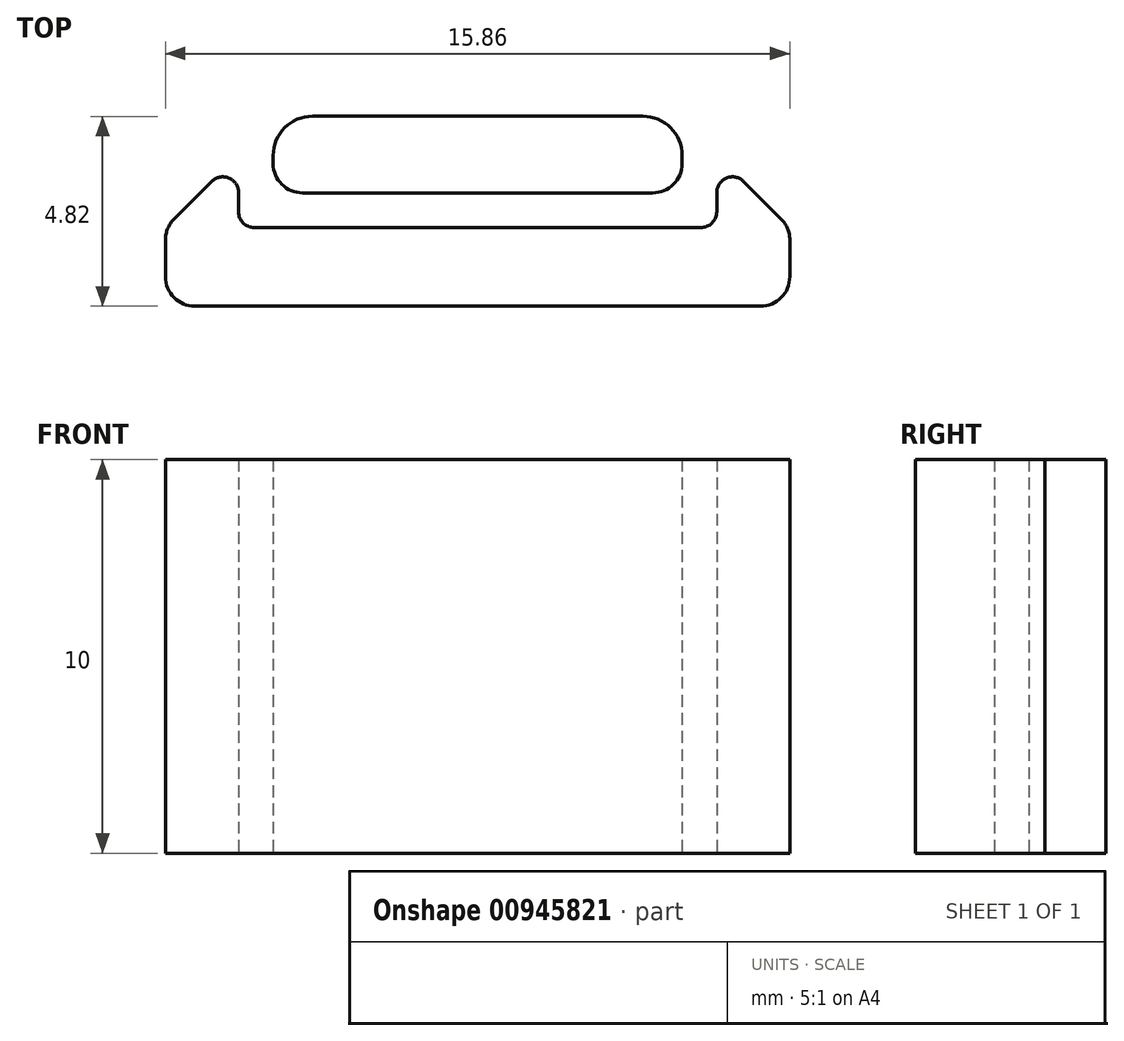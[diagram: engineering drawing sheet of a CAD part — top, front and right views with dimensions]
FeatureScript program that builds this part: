
annotation { "Feature Type Name" : "Feature", "Feature Type Description" : "" }
export const myFeature = defineFeature(function(context is Context, id is Id, definition is map)
    precondition{}
    {
        {
            var Q0;
            Q0=qCreatedBy(makeId("Top.planeOp"),FACE);
            var sketch = newSketch(context, id + "F0", { "sketchPlane" : qUnion([Q0])});
            skLineSegment(sketch, "E0.bottom", {"start": v(5.2, -0.97) * mm, "end": v(-5.2, -0.98) * mm});
            skLineSegment(sketch, "E0.top", {"start": v(5.2, 0.98) * mm, "end": v(-5.2, 0.97) * mm});
            skLineSegment(sketch, "E0.left", {"start": v(5.2, -0.97) * mm, "end": v(5.2, 0.98) * mm});
            skLineSegment(sketch, "E0.right", {"start": v(-5.2, -0.98) * mm, "end": v(-5.2, 0.97) * mm});
            skPoint(sketch, "E0.middle", {"position": v(0, 0) * mm});
            skLineSegment(sketch, "E1.bottom", {"start": v(6.08, -1.85) * mm, "end": v(-6.07, -1.86) * mm});
            skLineSegment(sketch, "E1.top", {"start": v(6.07, 1.86) * mm, "end": v(-6.08, 1.85) * mm});
            skLineSegment(sketch, "E1.left", {"start": v(6.08, -1.85) * mm, "end": v(6.08, 1.86) * mm});
            skLineSegment(sketch, "E1.right", {"start": v(-6.07, -1.86) * mm, "end": v(-6.07, 1.85) * mm});
            skLineSegment(sketch, "E2", {"start": v(-6.07, 0) * mm, "end": v(-7.93, -1.86) * mm});
            skLineSegment(sketch, "E3", {"start": v(6.07, 0) * mm, "end": v(7.93, -1.86) * mm});
            skLineSegment(sketch, "E4.bottom", {"start": v(-7.93, -1.86) * mm, "end": v(7.93, -1.86) * mm});
            skLineSegment(sketch, "E4.top", {"start": v(-7.93, -3.86) * mm, "end": v(7.93, -3.86) * mm});
            skLineSegment(sketch, "E4.left", {"start": v(-7.93, -1.86) * mm, "end": v(-7.93, -3.86) * mm});
            skLineSegment(sketch, "E4.right", {"start": v(7.93, -1.86) * mm, "end": v(7.93, -3.86) * mm});
            skSolve(sketch);
        }
        {
            var Q0;
            Q0=makeQuery(id+"F0.imprint","IMPRINT",FACE,{"disambiguationData":[TD([[makeQuery(id+"F0.imprint","IMPRINT",EDGE,{"derivedFrom":sQuery(id+"F0.wireOp",EDGE,"E0.bottom")}),-1.0]])]});
            var Q1;
            {var subQ3=sQuery(id+"F0.wireOp",EDGE,"E2");Q1=makeQuery(id+"F0.imprint","IMPRINT",FACE,{"disambiguationData":[TD([[makeQuery(id+"F0.imprint","IMPRINT",EDGE,{"derivedFrom":subQ3}),1.0]])]});}
            var Q2;
            Q2=makeQuery(id+"F0.imprint","IMPRINT",FACE,{"disambiguationData":[TD([[makeQuery(id+"F0.imprint","IMPRINT",EDGE,{"derivedFrom":sQuery(id+"F0.wireOp",EDGE,"E4.top")}),1.0]])]});
            var Q3;
            {var subQ3=sQuery(id+"F0.wireOp",EDGE,"E3");Q3=makeQuery(id+"F0.imprint","IMPRINT",FACE,{"disambiguationData":[TD([[makeQuery(id+"F0.imprint","IMPRINT",EDGE,{"derivedFrom":subQ3}),-1.0]])]});}
            extrude(context, id + "F1", {"entities" : qUnion([Q0, Q1, Q2, Q3]), "depth" : 10 * mm, "offsetDistance" : 25 * mm});
        }
        {
            var Q0;
            Q0=makeQuery(id+"F1.opExtrude","SWEPT_EDGE",EDGE,{"disambiguationData":[OSD([sQuery(id+"F0.wireOp",EDGE,"E0.bottom"),sQuery(id+"F0.wireOp",EDGE,"E0.right")])]});
            var Q1;
            Q1=makeQuery(id+"F1.opExtrude","SWEPT_EDGE",EDGE,{"disambiguationData":[OSD([sQuery(id+"F0.wireOp",EDGE,"E0.bottom"),sQuery(id+"F0.wireOp",EDGE,"E0.left")])]});
            var Q2;
            Q2=makeQuery(id+"F1.opExtrude","SWEPT_EDGE",EDGE,{"disambiguationData":[OSD([sQuery(id+"F0.wireOp",EDGE,"E4.top"),sQuery(id+"F0.wireOp",EDGE,"E4.left")])]});
            var Q3;
            Q3=makeQuery(id+"F1.opExtrude","SWEPT_EDGE",EDGE,{"disambiguationData":[OSD([sQuery(id+"F0.wireOp",EDGE,"E4.top"),sQuery(id+"F0.wireOp",EDGE,"E4.right")])]});
            var Q4;
            Q4=makeQuery(id+"F1.opExtrude","SWEPT_EDGE",EDGE,{"disambiguationData":[OSD([sQuery(id+"F0.wireOp",EDGE,"E3"),sQuery(id+"F0.wireOp",EDGE,"E4.bottom"),sQuery(id+"F0.wireOp",EDGE,"E4.right")])]});
            var Q5;
            Q5=makeQuery(id+"F1.opExtrude","SWEPT_EDGE",EDGE,{"disambiguationData":[OSD([sQuery(id+"F0.wireOp",EDGE,"E2"),sQuery(id+"F0.wireOp",EDGE,"E4.bottom"),sQuery(id+"F0.wireOp",EDGE,"E4.left")])]});
            fillet(context, id + "F2", {"entities" : qUnion([Q0, Q1, Q2, Q3, Q4, Q5]), "radius" : 0.75 * mm, "tangentPropagation" : true, "allowEdgeOverflow" : false});
        }
        {
            var Q0;
            Q0=makeQuery(id+"F1.opExtrude","SWEPT_EDGE",EDGE,{"disambiguationData":[OSD([sQuery(id+"F0.wireOp",EDGE,"E1.right"),sQuery(id+"F0.wireOp",EDGE,"E2")])]});
            var Q1;
            Q1=makeQuery(id+"F1.opExtrude","SWEPT_EDGE",EDGE,{"disambiguationData":[OSD([sQuery(id+"F0.wireOp",EDGE,"E1.left"),sQuery(id+"F0.wireOp",EDGE,"E3")])]});
            var Q2;
            Q2=makeQuery(id+"F1.opExtrude","SWEPT_EDGE",EDGE,{"disambiguationData":[OSD([sQuery(id+"F0.wireOp",EDGE,"E1.left"),sQuery(id+"F0.wireOp",EDGE,"E4.bottom")])]});
            var Q3;
            Q3=makeQuery(id+"F1.opExtrude","SWEPT_EDGE",EDGE,{"disambiguationData":[OSD([sQuery(id+"F0.wireOp",EDGE,"E1.right"),sQuery(id+"F0.wireOp",EDGE,"E4.bottom")])]});
            fillet(context, id + "F3", {"entities" : qUnion([Q0, Q1, Q2, Q3]), "radius" : 0.4 * mm, "tangentPropagation" : true, "allowEdgeOverflow" : false});
        }
        {
            var Q0;
            Q0=makeQuery(id+"F1.opExtrude","SWEPT_EDGE",EDGE,{"disambiguationData":[OSD([sQuery(id+"F0.wireOp",EDGE,"E0.top"),sQuery(id+"F0.wireOp",EDGE,"E0.right")])]});
            var Q1;
            Q1=makeQuery(id+"F1.opExtrude","SWEPT_EDGE",EDGE,{"disambiguationData":[OSD([sQuery(id+"F0.wireOp",EDGE,"E0.top"),sQuery(id+"F0.wireOp",EDGE,"E0.left")])]});
            fillet(context, id + "F4", {"entities" : qUnion([Q0, Q1]), "radius" : 1 * mm, "tangentPropagation" : true, "allowEdgeOverflow" : false});
        }
    });
